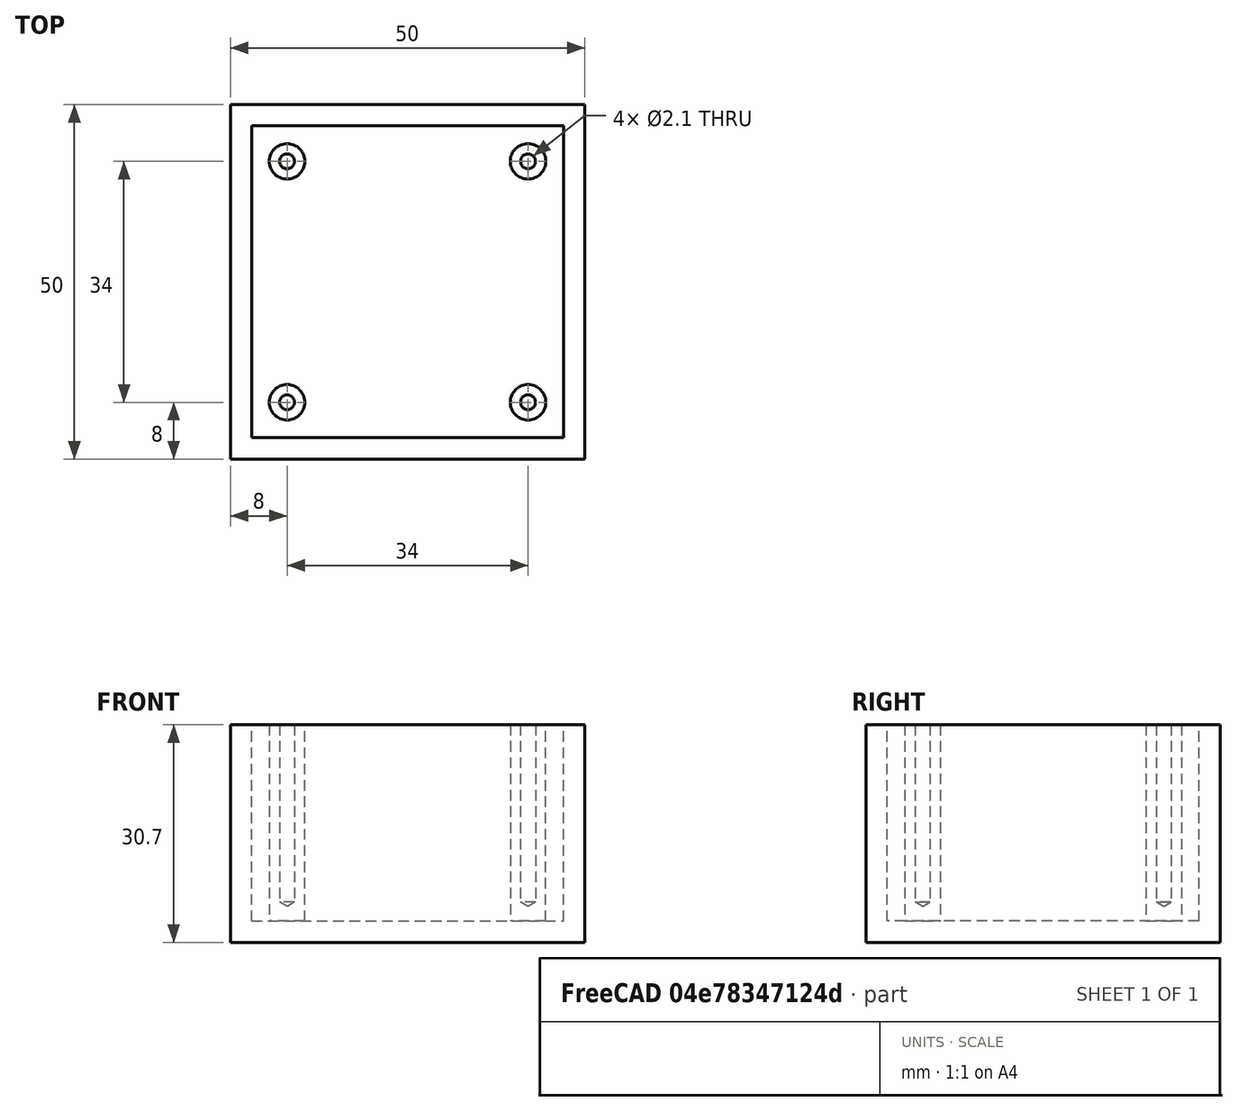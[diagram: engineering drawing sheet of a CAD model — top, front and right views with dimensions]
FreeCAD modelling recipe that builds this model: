
FCSTD DOCUMENT  (FreeCAD 0.21R33771 (Git))
Label: part1
License: All rights reserved
LicenseURL: http://en.wikipedia.org/wiki/All_rights_reserved
objects: TechDraw::DrawViewDimension×9, Sketcher::SketchObject×4, PartDesign::Pad×3, TechDraw::DrawProjGroupItem×3, PartDesign::Hole×1, PartDesign::Body×1, TechDraw::DrawSVGTemplate×1, TechDraw::DrawViewPart×1, TechDraw::DrawProjGroup×1, TechDraw::DrawPage×1
note: 27 computed .brp shape members not serialized (recipe doc carries the construction recipe); baked Part::Feature solids carry a one-line shape summary decoded from their .brp

FEATURE [Sketcher::SketchObject] Sketch
  FullyConstrained = true
  MapMode = 5
  Support = -> [XY_Plane]
  sketch-geometry (5):
    g0: LineSegment StartX=-25 StartY=-25 StartZ=0 EndX=-25 EndY=25 EndZ=0
    g1: LineSegment StartX=-25 StartY=25 StartZ=0 EndX=25 EndY=25 EndZ=0
    g2: LineSegment StartX=25 StartY=25 StartZ=0 EndX=25 EndY=-25 EndZ=0
    g3: LineSegment StartX=25 StartY=-25 StartZ=0 EndX=-25 EndY=-25 EndZ=0
    g4: GeomPoint X=0 Y=0 Z=0
  constraints (12):
    c: Coincident(g0,g1)
    c: Coincident(g1,g2)
    c: Coincident(g2,g3)
    c: Coincident(g3,g0)
    c: Horizontal(g1)
    c: Horizontal(g3)
    c: Vertical(g0)
    c: Vertical(g2)
    c: Symmetric(g1,g0,g4)
    c: Coincident(g4,g-1)
    c: DistanceX(g1,g1) = 50
    c: DistanceY(g0,g0) = 50
FEATURE [PartDesign::Pad] Pad
  Direction = (0,0,1)
  Length = 3
  Length2 = 10
  Profile = -> Sketch
  ReferenceAxis = -> Sketch [N_Axis]
  Type = 0
FEATURE [Sketcher::SketchObject] Sketch001
  ExternalGeometry = -> [Pad]
  FullyConstrained = true
  MapMode = 5
  Placement = pos=(0,0,3) rot=(0,0,1;0rad)
  Support = -> [Pad]
  sketch-geometry (8):
    g0: LineSegment StartX=-25 StartY=25 StartZ=0 EndX=25 EndY=25 EndZ=0
    g1: LineSegment StartX=25 StartY=25 StartZ=0 EndX=25 EndY=-25 EndZ=0
    g2: LineSegment StartX=25 StartY=-25 StartZ=0 EndX=-25 EndY=-25 EndZ=0
    g3: LineSegment StartX=-25 StartY=-25 StartZ=0 EndX=-25 EndY=25 EndZ=0
    g4: LineSegment StartX=-22 StartY=22 StartZ=0 EndX=22 EndY=22 EndZ=0
    g5: LineSegment StartX=22 StartY=22 StartZ=0 EndX=22 EndY=-22 EndZ=0
    g6: LineSegment StartX=22 StartY=-22 StartZ=0 EndX=-22 EndY=-22 EndZ=0
    g7: LineSegment StartX=-22 StartY=-22 StartZ=0 EndX=-22 EndY=22 EndZ=0
  constraints (22):
    c: Coincident(g0,g1)
    c: Coincident(g1,g2)
    c: Coincident(g2,g3)
    c: Coincident(g3,g0)
    c: Horizontal(g0)
    c: Horizontal(g2)
    c: Vertical(g1)
    c: Vertical(g3)
    c: Coincident(g0,g-3)
    c: Coincident(g1,g-4)
    c: Coincident(g4,g5)
    c: Coincident(g5,g6)
    c: Coincident(g6,g7)
    c: Coincident(g7,g4)
    c: Horizontal(g4)
    c: Horizontal(g6)
    c: Vertical(g5)
    c: Vertical(g7)
    c: DistanceY(g4,g0) = 3
    c: DistanceX(g0,g4) = 3
    c: DistanceX(g5,g1) = 3
    c: DistanceY(g1,g5) = 3
FEATURE [PartDesign::Pad] Pad001
  BaseFeature = -> Pad
  Direction = (0,0,1)
  Length = 27.7
  Length2 = 10
  Profile = -> Sketch001
  ReferenceAxis = -> Sketch001 [N_Axis]
  Refine = true
  Type = 0
FEATURE [Sketcher::SketchObject] Sketch002
  ExternalGeometry = -> [Pad001]
  FullyConstrained = true
  MapMode = 5
  Placement = pos=(0,0,3) rot=(0,0,1;0rad)
  Support = -> [Pad001]
  sketch-geometry (4):
    g0: Circle CenterX=-17 CenterY=17 CenterZ=0 NormalX=0 NormalY=0 NormalZ=1 AngleXU=0 Radius=2.5
    g1: Circle CenterX=17 CenterY=17 CenterZ=0 NormalX=0 NormalY=0 NormalZ=1 AngleXU=0 Radius=2.5
    g2: Circle CenterX=17 CenterY=-17 CenterZ=0 NormalX=0 NormalY=0 NormalZ=1 AngleXU=0 Radius=2.5
    g3: Circle CenterX=-17 CenterY=-17 CenterZ=0 NormalX=0 NormalY=0 NormalZ=1 AngleXU=0 Radius=2.5
  constraints (12):
    c: Equal(g0,g1)
    c: Equal(g1,g2)
    c: Equal(g2,g3)
    c: Diameter(g0) = 5
    c: Horizontal(g0,g1)
    c: Horizontal(g3,g2)
    c: Vertical(g0,g3)
    c: Vertical(g1,g2)
    c: DistanceY(g0,g-3) = 5
    c: DistanceX(g-3,g0) = 5
    c: DistanceX(g2,g-4) = 5
    c: DistanceY(g-4,g2) = 5
FEATURE [PartDesign::Pad] Pad002
  BaseFeature = -> Pad001
  Direction = (0,0,1)
  Length = 27.7
  Length2 = 10
  Profile = -> Sketch002
  ReferenceAxis = -> Sketch002 [N_Axis]
  Type = 0
FEATURE [Sketcher::SketchObject] Sketch003
  ExternalGeometry = -> [Pad002]
  FullyConstrained = true
  MapMode = 5
  Placement = pos=(0,0,30.7) rot=(0,0,1;0rad)
  Support = -> [Pad002]
  sketch-geometry (4):
    g0: Circle CenterX=-17 CenterY=17 CenterZ=0 NormalX=0 NormalY=0 NormalZ=1 AngleXU=0 Radius=1
    g1: Circle CenterX=17 CenterY=17 CenterZ=0 NormalX=0 NormalY=0 NormalZ=1 AngleXU=0 Radius=1
    g2: Circle CenterX=-17 CenterY=-17 CenterZ=0 NormalX=0 NormalY=0 NormalZ=1 AngleXU=0 Radius=1
    g3: Circle CenterX=17 CenterY=-17 CenterZ=0 NormalX=0 NormalY=0 NormalZ=1 AngleXU=0 Radius=1
  constraints (8):
    c: Coincident(g0,g-3)
    c: Diameter(g0) = 2
    c: Coincident(g1,g-4)
    c: Coincident(g2,g-6)
    c: Coincident(g3,g-5)
    c: Equal(g2,g3)
    c: Equal(g3,g1)
    c: Equal(g1,g0)
FEATURE [PartDesign::Hole] Hole
  BaseFeature = -> Pad002
  CustomThreadClearance = 0
  Depth = 25
  DepthType = 0
  Diameter = 2.1
  DrillForDepth = false
  DrillPoint = 1
  DrillPointAngle = 118
  HoleCutCountersinkAngle = 90
  HoleCutCustomValues = false
  HoleCutDepth = 0
  HoleCutDiameter = 6.1
  HoleCutType = 0
  ModelThread = true
  Profile = -> Sketch003
  Tapered = false
  TaperedAngle = 90
  ThreadClass = 0
  ThreadDepth = 25
  ThreadDepthType = 0
  ThreadDirection = 0
  ThreadFit = 0
  ThreadSize = 5
  ThreadType = 1
  Threaded = false
  UseCustomThreadClearance = false
FEATURE [PartDesign::Body] Body
  Group = -> [Sketch,Pad,Sketch001,Pad001,Sketch002,Pad002,Sketch003,Hole]
  Origin = -> Origin
  Tip = -> Hole
FEATURE [TechDraw::DrawSVGTemplate] Template
  EditableTexts = Designed_by_Name=Designed by Name; Drawing_number=Drawing number; FC-Date=Date; FC-SC=Scale; FC-SH=Sheet; FC-Title=Item #5 (part 1); Subtitle=Subtitle; Weight=Weight
  Height = 210
  Orientation = 1
  Template = <path>
  Width = 297
FEATURE [TechDraw::DrawViewPart] View
  CoarseView = false
  Direction = (0.57735,-0.57735,0.57735)
  Focus = 100
  HardHidden = false
  IsoCount = 0
  IsoHidden = false
  IsoVisible = false
  LockPosition = false
  Perspective = false
  Rotation = 0
  ScaleType = 0
  ScrubCount = 0
  SeamHidden = false
  SeamVisible = false
  SmoothHidden = false
  SmoothVisible = true
  Source = -> [Hole]
  X = 67.0716
  XDirection = (0.707107,0.707107,0)
  Y = 143.645
FEATURE [TechDraw::DrawProjGroupItem] ProjItem  label="Front"
  Caption = Top View
  CoarseView = false
  Direction = (0,0,1)
  Focus = 100
  HardHidden = false
  IsoCount = 0
  IsoHidden = false
  IsoVisible = false
  LockPosition = true
  Perspective = false
  Rotation = 0
  RotationVector = (1,0,0)
  ScaleType = 2
  ScrubCount = 0
  SeamHidden = false
  SeamVisible = false
  SmoothHidden = false
  SmoothVisible = true
  Source = -> [Hole]
  Type = 0
  X = 0
  XDirection = (1,0,0)
  Y = 0
FEATURE [TechDraw::DrawProjGroupItem] ProjItem002  label="Bottom"
  Caption = Front View
  CoarseView = false
  Direction = (0,-1,0)
  Focus = 100
  HardHidden = false
  IsoCount = 0
  IsoHidden = false
  IsoVisible = false
  LockPosition = false
  Perspective = false
  Rotation = 0
  RotationVector = (1,0,0)
  ScaleType = 2
  ScrubCount = 0
  SeamHidden = false
  SeamVisible = false
  SmoothHidden = false
  SmoothVisible = true
  Source = -> [Hole]
  Type = 5
  X = 0
  XDirection = (1,0,0)
  Y = 65.35
FEATURE [TechDraw::DrawProjGroupItem] ProjItem003  label="Right"
  Caption = Side View
  CoarseView = false
  Direction = (1,0,1e-16)
  Focus = 100
  HardHidden = false
  IsoCount = 0
  IsoHidden = false
  IsoVisible = false
  LockPosition = false
  Perspective = false
  Rotation = 0
  RotationVector = (1,0,0)
  ScaleType = 2
  ScrubCount = 0
  SeamHidden = false
  SeamVisible = false
  SmoothHidden = false
  SmoothVisible = true
  Source = -> [Hole]
  Type = 2
  X = -60.35
  XDirection = (1e-16,0,-1)
  Y = 0
FEATURE [TechDraw::DrawProjGroup] ProjGroup
  Anchor = -> ProjItem
  AutoDistribute = true
  LockPosition = false
  ProjectionType = 0
  Rotation = 0
  ScaleType = 0
  Source = -> [Hole]
  Views = -> [ProjItem,ProjItem002,ProjItem003]
  X = 226.408
  Y = 104.691
  spacingX = 20
  spacingY = 25
FEATURE [TechDraw::DrawViewDimension] Dimension
  AngleOverride = false
  Arbitrary = false
  ArbitraryTolerances = false
  EqualTolerance = true
  ExtensionAngle = 0
  FormatSpec = %.2w
  FormatSpecOverTolerance = %+.2w
  FormatSpecUnderTolerance = %+.2w
  Inverted = false
  LineAngle = 0
  LockPosition = false
  MeasureType = 1
  OverTolerance = 0
  References2D = -> [ProjItem]
  Rotation = 0
  ScaleType = 0
  TheoreticalExact = false
  Type = 2
  UnderTolerance = 0
  X = -33.0381
  Y = 6.20989
FEATURE [TechDraw::DrawViewDimension] Dimension001
  AngleOverride = false
  Arbitrary = false
  ArbitraryTolerances = false
  EqualTolerance = true
  ExtensionAngle = 0
  FormatSpec = %.2w
  FormatSpecOverTolerance = %+.2w
  FormatSpecUnderTolerance = %+.2w
  Inverted = false
  LineAngle = 0
  LockPosition = false
  MeasureType = 1
  OverTolerance = 0
  References2D = -> [ProjItem]
  Rotation = 0
  ScaleType = 0
  TheoreticalExact = false
  Type = 1
  UnderTolerance = 0
  X = 0
  Y = 34.9198
FEATURE [TechDraw::DrawViewDimension] Dimension002
  AngleOverride = false
  Arbitrary = false
  ArbitraryTolerances = false
  EqualTolerance = true
  ExtensionAngle = 0
  FormatSpec = %.2w
  FormatSpecOverTolerance = %+.2w
  FormatSpecUnderTolerance = %+.2w
  Inverted = false
  LineAngle = 0
  LockPosition = false
  MeasureType = 1
  OverTolerance = 0
  References2D = -> [ProjItem]
  Rotation = 0
  ScaleType = 0
  TheoreticalExact = false
  Type = 1
  UnderTolerance = 0
  X = -33.9837
  Y = -29.0428
FEATURE [TechDraw::DrawViewDimension] Dimension003
  AngleOverride = false
  Arbitrary = false
  ArbitraryTolerances = false
  EqualTolerance = true
  ExtensionAngle = 0
  FormatSpec = ⌀%.2w
  FormatSpecOverTolerance = %+.2w
  FormatSpecUnderTolerance = %+.2w
  Inverted = false
  LineAngle = 0
  LockPosition = false
  MeasureType = 1
  OverTolerance = 0
  References2D = -> [ProjItem]
  Rotation = 0
  ScaleType = 0
  TheoreticalExact = false
  Type = 5
  UnderTolerance = 0
  X = -5.94876
  Y = 23.6
FEATURE [TechDraw::DrawViewDimension] Dimension004
  AngleOverride = false
  Arbitrary = false
  ArbitraryTolerances = false
  EqualTolerance = true
  ExtensionAngle = 0
  FormatSpec = ⌀%.2w
  FormatSpecOverTolerance = %+.2w
  FormatSpecUnderTolerance = %+.2w
  Inverted = false
  LineAngle = 0
  LockPosition = false
  MeasureType = 1
  OverTolerance = 0
  References2D = -> [ProjItem]
  Rotation = 0
  ScaleType = 0
  TheoreticalExact = false
  Type = 5
  UnderTolerance = 0
  X = -4.48595
  Y = 15.3108
FEATURE [TechDraw::DrawViewDimension] Dimension005
  AngleOverride = false
  Arbitrary = false
  ArbitraryTolerances = false
  EqualTolerance = true
  ExtensionAngle = 0
  FormatSpec = %.2w
  FormatSpecOverTolerance = %+.2w
  FormatSpecUnderTolerance = %+.2w
  Inverted = false
  LineAngle = 0
  LockPosition = false
  MeasureType = 1
  OverTolerance = 0
  References2D = -> [ProjItem]
  Rotation = 0
  ScaleType = 0
  TheoreticalExact = false
  Type = 1
  UnderTolerance = 0
  X = 20.5124
  Y = 11.8099
FEATURE [TechDraw::DrawViewDimension] Dimension006
  AngleOverride = false
  Arbitrary = false
  ArbitraryTolerances = false
  EqualTolerance = true
  ExtensionAngle = 0
  FormatSpec = %.2w
  FormatSpecOverTolerance = %+.2w
  FormatSpecUnderTolerance = %+.2w
  Inverted = false
  LineAngle = 0
  LockPosition = false
  MeasureType = 1
  OverTolerance = 0
  References2D = -> [ProjItem]
  Rotation = 0
  ScaleType = 0
  TheoreticalExact = false
  Type = 2
  UnderTolerance = 0
  X = 29.9843
  Y = 24.1826
FEATURE [TechDraw::DrawViewDimension] Dimension007
  AngleOverride = false
  Arbitrary = false
  ArbitraryTolerances = false
  EqualTolerance = true
  ExtensionAngle = 0
  FormatSpec = %.2w
  FormatSpecOverTolerance = %+.2w
  FormatSpecUnderTolerance = %+.2w
  Inverted = false
  LineAngle = 0
  LockPosition = false
  MeasureType = 1
  OverTolerance = 0
  References2D = -> [ProjItem003]
  Rotation = 0
  ScaleType = 0
  TheoreticalExact = false
  Type = 1
  UnderTolerance = 0
  X = -0.516683
  Y = 41.9671
FEATURE [TechDraw::DrawViewDimension] Dimension008
  AngleOverride = false
  Arbitrary = false
  ArbitraryTolerances = false
  EqualTolerance = true
  ExtensionAngle = 0
  FormatSpec = %.2w
  FormatSpecOverTolerance = %+.2w
  FormatSpecUnderTolerance = %+.2w
  Inverted = false
  LineAngle = 0
  LockPosition = false
  MeasureType = 1
  OverTolerance = 0
  References2D = -> [ProjItem003]
  Rotation = 0
  ScaleType = 0
  TheoreticalExact = false
  Type = 1
  UnderTolerance = 0
  X = 13.075
  Y = 52.8175
FEATURE [TechDraw::DrawPage] Page
  KeepUpdated = true
  NextBalloonIndex = 1
  ProjectionType = 0
  Template = -> Template
  Views = -> [View,ProjGroup,Dimension,Dimension001,Dimension002,Dimension003,Dimension004,Dimension005,Dimension006,Dimension007,Dimension008]
note: 1 file-system path scrubbed to <path> (originals preserved in the JSON sidecar)
